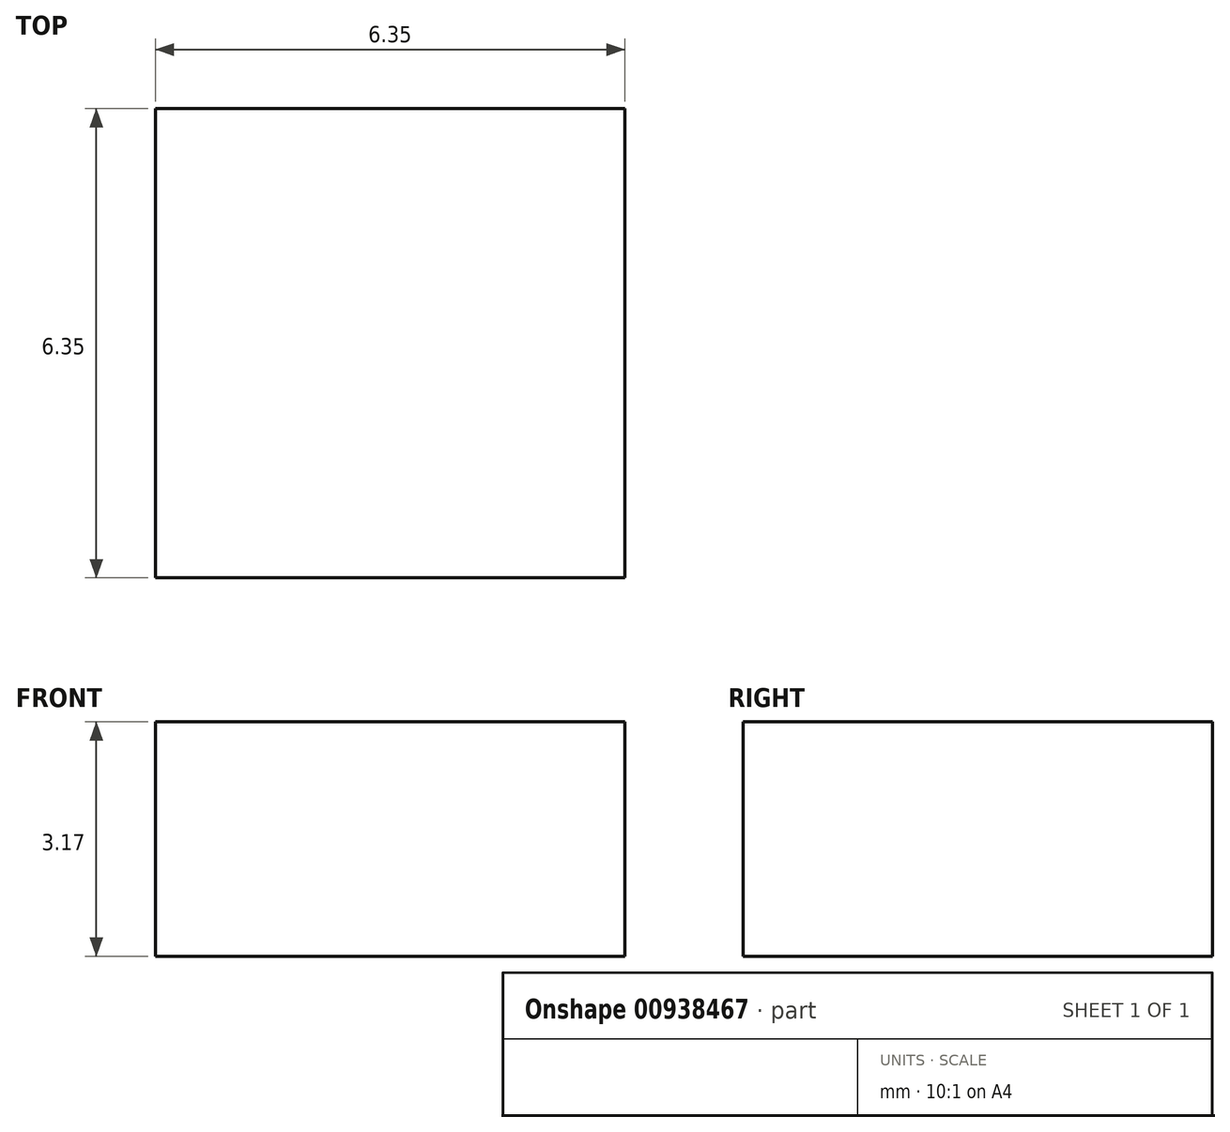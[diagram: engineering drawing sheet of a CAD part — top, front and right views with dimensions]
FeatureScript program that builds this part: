
annotation { "Feature Type Name" : "Feature", "Feature Type Description" : "" }
export const myFeature = defineFeature(function(context is Context, id is Id, definition is map)
    precondition{}
    {
        {
            var Q0;
            Q0=qCreatedBy(makeId("Top.planeOp"),FACE);
            var sketch = newSketch(context, id + "F0", { "sketchPlane" : qUnion([Q0])});
            skLineSegment(sketch, "E0.bottom", {"start": v(-6.35, 6.35) * mm, "end": v(0, 6.35) * mm});
            skLineSegment(sketch, "E0.top", {"start": v(-6.35, 0) * mm, "end": v(0, 0) * mm});
            skLineSegment(sketch, "E0.left", {"start": v(-6.35, 6.35) * mm, "end": v(-6.35, 0) * mm});
            skLineSegment(sketch, "E0.right", {"start": v(0, 6.35) * mm, "end": v(0, 0) * mm});
            skSolve(sketch);
        }
        {
            var Q0;
            Q0=makeQuery(id+"F0.imprint","IMPRINT",FACE,{"disambiguationData":[TD([[makeQuery(id+"F0.imprint","IMPRINT",EDGE,{"derivedFrom":sQuery(id+"F0.wireOp",EDGE,"E0.bottom")}),-1.0]])]});
            extrude(context, id + "F1", {"entities" : qUnion([Q0]), "depth" : 3.17 * mm, "offsetDistance" : 25.4 * mm});
        }
    });
